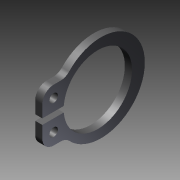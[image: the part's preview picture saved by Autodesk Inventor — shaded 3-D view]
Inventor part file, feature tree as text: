
AUTODESK INVENTOR PART (.ipt)
format: ipt  version: 2011 SP1 (Build 150282100, 282)  size: 127,488 bytes
history: native  units: mm
features: other x14, extrude x2, sketch x2
ambient origin geometry x8: Origin, YZ Plane, XZ Plane, XY Plane, X Axis, Y Axis, Z Axis, Center Point
bodies: Solid1 (feature_tree)
feature tree (18):
  extrude  "Extrusion1"  Depth=1.0mm TaperAngle=0.0deg
  extrude  "Extrusion2"  [1 undecoded]
  other  "1_XY"
  other  "1_YZ"
  other  "1_ZX"
  other  "1_X"
  other  "1_Y"
  other  "1_Z"
  other  "1_Center"
  other  "combination_module_XY"
  other  "combination_module_YZ"
  other  "combination_module_ZX"
  other  "combination_module_X"
  other  "combination_module_Y"
  other  "combination_module_Z"
  other  "combination_module_Center"
  sketch  "Sketch_5"  dims[d0=1.0mm d1=0.0mm d2=1.0mm d3=0.0mm]
  sketch  "Sketch_6"  dims[d4=0.0mm]
note: 1 required parameter value undecoded (feature->parameter linkage not recoverable at this tier; creation-order binding heuristic only, values carry confidence <= 0.55)
